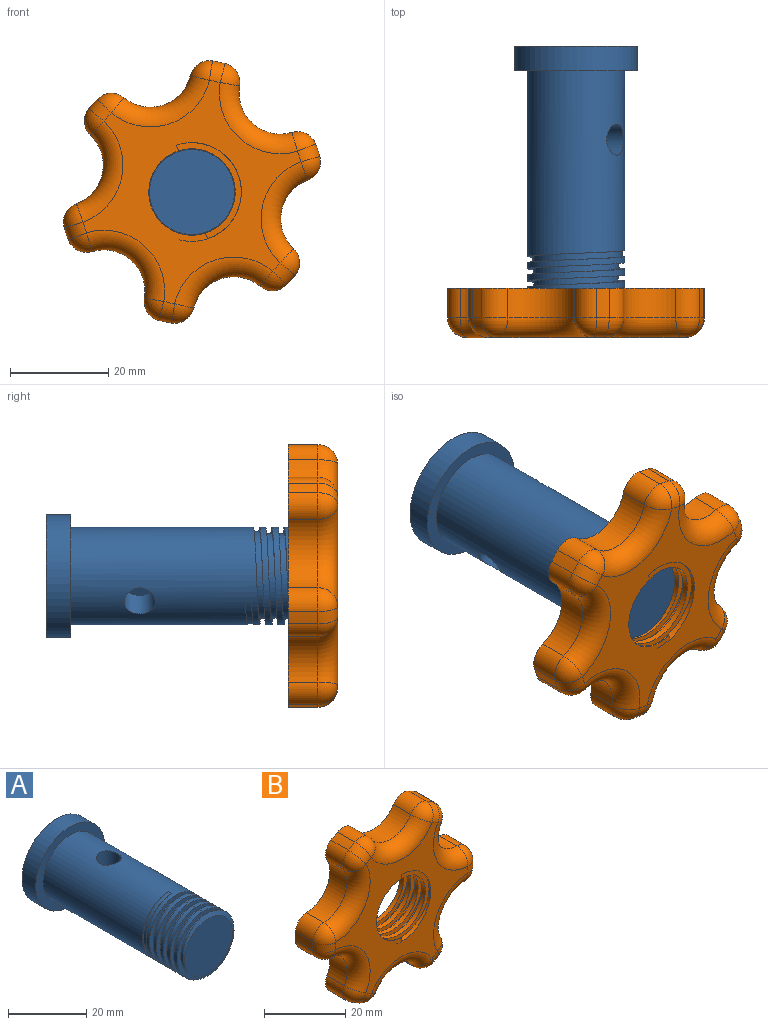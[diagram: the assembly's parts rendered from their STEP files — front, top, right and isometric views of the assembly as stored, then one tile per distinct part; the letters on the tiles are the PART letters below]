
ASSEMBLY  parts=2 mates=1
PART A: 36 faces, bbox 25x55.1x25 mm
  f0: plane 17.3x17.3mm, normal (0,-1,0), area 235.1mm2, adj f29,f33
  f1: cylinder r=9.9mm len=40.5mm, axis (0,1,0), area 2300.5mm2, adj f6,f14,f27,f28,f31,f32,f34,f35
  f2: cylinder r=9.9mm len=3.14mm, axis (0,1,0), area 0.2mm2, adj f3,f30,f33
  f3: cylinder r=9.9mm len=19.8mm, axis (0,1,0), area 62mm2, adj f2,f4,f30,f31,f33
  f4: cylinder r=9.9mm len=19.8mm, axis (0,1,0), area 77.7mm2, adj f3,f5,f30,f31
  f5: cylinder r=9.9mm len=19.8mm, axis (0,1,0), area 77.7mm2, adj f4,f6,f30,f31
  f6: cylinder r=9.9mm len=19.8mm, axis (0,1,0), area 77.8mm2, adj f1,f5,f30,f31
  f7: plane 2.45x0.1mm, normal (0,1,0), area 0.2mm2, adj f9,f19,f23,f24
  f8: plane 2.45x0.1mm, normal (0,1,0), area 0.2mm2, adj f11,f16,f25,f26
  f9: plane 42x13.1mm, normal (0,0,1), area 496.2mm2, adj f7,f10,f12,f13,f18,f20,f22,f23
  f10: cylinder r=2.55mm len=42mm, axis (0,1,0), area 336.5mm2, adj f9,f11,f13,f22
  f11: plane 42x13.1mm, normal (0,0,-1), area 496.2mm2, adj f8,f10,f12,f13,f15,f17,f22,f25
  f12: cylinder r=2.55mm len=42mm, axis (0,1,0), area 336.5mm2, adj f9,f11,f13,f22
  f13: plane 18.2x5.1mm, normal (0,1,0), area 87.2mm2, adj f9,f10,f11,f12
  f14: plane 25x25mm, normal (0,-1,0), area 183mm2, adj f1,f21
  f15: plane 2.5x2.45mm, normal (1,0,0), area 6.1mm2, adj f11,f16,f22,f26
  f16: plane 5.1x5mm, normal (0,0,-1), area 22.8mm2, adj f8,f15,f17,f22,f25,f26
  f17: plane 2.5x2.45mm, normal (-1,0,0), area 6.1mm2, adj f11,f16,f22,f25
  f18: plane 2.5x2.45mm, normal (-1,0,0), area 6.1mm2, adj f9,f19,f22,f24
  f19: plane 5.1x5mm, normal (0,0,1), area 22.8mm2, adj f7,f18,f20,f22,f23,f24
  f20: plane 2.5x2.45mm, normal (1,0,0), area 6.1mm2, adj f9,f19,f22,f23
  f21: cylinder r=12.5mm len=25mm, axis (0,-1,0), area 392.7mm2, adj f14,f22
  f22: plane 25x25mm, normal (0,1,0), area 378.6mm2, adj f9,f10,f11,f12,f15,f16,f17,f18
  f23: cylinder r=2.5mm len=2.5mm, axis (0,0,1), area 9.6mm2, adj f7,f9,f19,f20
  f24: cylinder r=2.5mm len=2.5mm, axis (0,0,-1), area 9.6mm2, adj f7,f9,f18,f19
  f25: cylinder r=2.5mm len=2.5mm, axis (0,0,-1), area 9.6mm2, adj f8,f11,f16,f17
  f26: cylinder r=2.5mm len=2.5mm, axis (0,0,1), area 9.6mm2, adj f8,f11,f15,f16
  f27: bspline ~21.75x21.21mm, area 37.3mm2, adj f1,f30,f32
  f28: bspline ~21.75x21.21mm, area 37.3mm2, adj f1,f31,f32
  f29: cylinder r=8.65mm len=17.3mm, axis (0,-1,0), area 310.1mm2, adj f0,f30,f31,f32
  f30: bspline ~22.86x19.8mm, area 304.2mm2, adj f2,f3,f4,f5,f6,f27,f29,f33
  f31: bspline ~22.86x19.8mm, area 340.6mm2, adj f1,f3,f4,f5,f6,f28,f29,f33
  f32: bspline ~19.24x18.69mm, area 72.8mm2, adj f1,f27,f28,f29
  f33: cone r=9.9mm half-angle=63.4deg, axis (0,1,0), area 40.7mm2, adj f0,f2,f3,f30,f31
  f34: cylinder r=3.15mm len=7.35mm, axis (0,0,1), area 145.5mm2, adj f1,f11
  f35: cylinder r=3.15mm len=6.84mm, axis (0,0,1), area 135.3mm2, adj f1,f9
PART B: 54 faces, bbox 54.1x10.4x48.9 mm
  f0: cylinder r=10.05mm len=20.1mm, axis (0,1,0), area 317.1mm2, adj f25,f26,f52,f53
  f1: cylinder r=8.39mm len=12.33mm, axis (0,1,0), area 102mm2, adj f2,f24,f26,f34
  f2: cylinder r=4mm len=6mm, axis (0,1,0), area 35.7mm2, adj f1,f3,f26,f32
  f3: cylinder r=27mm len=6mm, axis (0,1,0), area 15.8mm2, adj f2,f4,f26,f30
  f4: cylinder r=4mm len=6mm, axis (0,1,0), area 35.7mm2, adj f3,f5,f26,f28
  f5: cylinder r=8.39mm len=12.33mm, axis (0,1,0), area 102mm2, adj f4,f6,f26,f27
  f6: cylinder r=4mm len=6mm, axis (0,1,0), area 35.7mm2, adj f5,f7,f26,f29
  f7: cylinder r=27mm len=6mm, axis (0,1,0), area 15.8mm2, adj f6,f8,f26,f31
  f8: cylinder r=4mm len=6mm, axis (0,1,0), area 35.7mm2, adj f7,f9,f26,f33
  f9: cylinder r=8.39mm len=14.24mm, axis (0,1,0), area 102mm2, adj f8,f10,f26,f35
  f10: cylinder r=4mm len=6mm, axis (0,1,0), area 35.7mm2, adj f9,f11,f26,f37
  f11: cylinder r=27mm len=6mm, axis (0,1,0), area 15.8mm2, adj f10,f12,f26,f39
  f12: cylinder r=4mm len=6mm, axis (0,1,0), area 35.7mm2, adj f11,f13,f26,f41
  f13: cylinder r=8.39mm len=12.33mm, axis (0,1,0), area 102mm2, adj f12,f14,f26,f43
  f14: cylinder r=4mm len=6mm, axis (0,1,0), area 35.7mm2, adj f13,f15,f26,f45
  f15: cylinder r=27mm len=6mm, axis (0,1,0), area 15.8mm2, adj f14,f16,f26,f47
  f16: cylinder r=4mm len=6mm, axis (0,1,0), area 35.7mm2, adj f15,f17,f26,f49
  f17: cylinder r=8.39mm len=12.33mm, axis (0,1,0), area 102mm2, adj f16,f18,f26,f50
  f18: cylinder r=4mm len=6mm, axis (0,1,0), area 35.7mm2, adj f17,f19,f26,f48
  f19: cylinder r=27mm len=6mm, axis (0,1,0), area 15.8mm2, adj f18,f20,f26,f46
  f20: cylinder r=4mm len=6mm, axis (0,1,0), area 35.7mm2, adj f19,f21,f26,f44
  f21: cylinder r=8.39mm len=14.24mm, axis (0,1,0), area 102mm2, adj f20,f22,f26,f42
  f22: cylinder r=4mm len=6mm, axis (0,1,0), area 35.7mm2, adj f21,f23,f26,f40
  f23: cylinder r=27mm len=6mm, axis (0,1,0), area 15.8mm2, adj f22,f24,f26,f38
  f24: cylinder r=4mm len=6mm, axis (0,1,0), area 35.7mm2, adj f1,f23,f26,f36
  f25: plane 46x40.91mm, normal (0,-1,0), area 644.6mm2, adj f0,f27,f30,f31,f34,f35,f38,f39
  f26: plane 54x48.91mm, normal (0,1,0), area 1351.6mm2, adj f0,f1,f2,f3,f4,f5,f6,f7
  f27: torus R=12.39mm, axis (0,-1,0), area 125.4mm2, adj f5,f25,f28,f29
  f28: sphere r=4mm, area 23.8mm2, adj f4,f27,f30
  f29: sphere r=4mm, area 23.8mm2, adj f6,f27,f31
  f30: torus R=23mm, axis (0,-1,0), area 15.7mm2, adj f3,f25,f28,f32
  f31: torus R=23mm, axis (0,-1,0), area 15.7mm2, adj f7,f25,f29,f33
  f32: sphere r=4mm, area 23.8mm2, adj f2,f30,f34
  f33: sphere r=4mm, area 23.8mm2, adj f8,f31,f35
  f34: torus R=12.39mm, axis (0,-1,0), area 125.4mm2, adj f1,f25,f32,f36
  f35: torus R=12.39mm, axis (0,-1,0), area 125.4mm2, adj f9,f25,f33,f37
  f36: sphere r=4mm, area 23.8mm2, adj f24,f34,f38
  f37: sphere r=4mm, area 23.8mm2, adj f10,f35,f39
  f38: torus R=23mm, axis (0,-1,0), area 15.7mm2, adj f23,f25,f36,f40
  f39: torus R=23mm, axis (0,-1,0), area 15.7mm2, adj f11,f25,f37,f41
  f40: sphere r=4mm, area 23.8mm2, adj f22,f38,f42
  f41: sphere r=4mm, area 23.8mm2, adj f12,f39,f43
  f42: torus R=12.39mm, axis (0,-1,0), area 125.4mm2, adj f21,f25,f40,f44
  f43: torus R=12.39mm, axis (0,-1,0), area 125.4mm2, adj f13,f25,f41,f45
  f44: sphere r=4mm, area 23.8mm2, adj f20,f42,f46
  f45: sphere r=4mm, area 23.8mm2, adj f14,f43,f47
  f46: torus R=23mm, axis (0,-1,0), area 15.7mm2, adj f19,f25,f44,f48
  f47: torus R=23mm, axis (0,-1,0), area 15.7mm2, adj f15,f25,f45,f49
  f48: sphere r=4mm, area 23.8mm2, adj f18,f46,f50
  f49: sphere r=4mm, area 23.8mm2, adj f16,f47,f50
  f50: torus R=12.39mm, axis (0,-1,0), area 125.4mm2, adj f17,f25,f48,f49
  f51: cylinder r=8.8mm len=17.6mm, axis (0,-1,0), area 277.7mm2, adj f25,f26,f52,f53
  f52: bspline ~23.21x20.1mm, area 296.6mm2, adj f0,f25,f26,f51
  f53: bspline ~23.21x20.1mm, area 296.6mm2, adj f0,f25,f26,f51
PLACE A rot(axis=(0,-1,0),122.6deg) t=(-62.47,5.45,-24.34)mm fixed
PLACE B rot(axis=(0,-1,0),18.3deg) t=(-62.47,-38.82,-24.34)mm
MATE cylindrical B.f11 <-> A.f1  axis (0,-1,0) through (-62.47,-48.82,-24.34)mm
